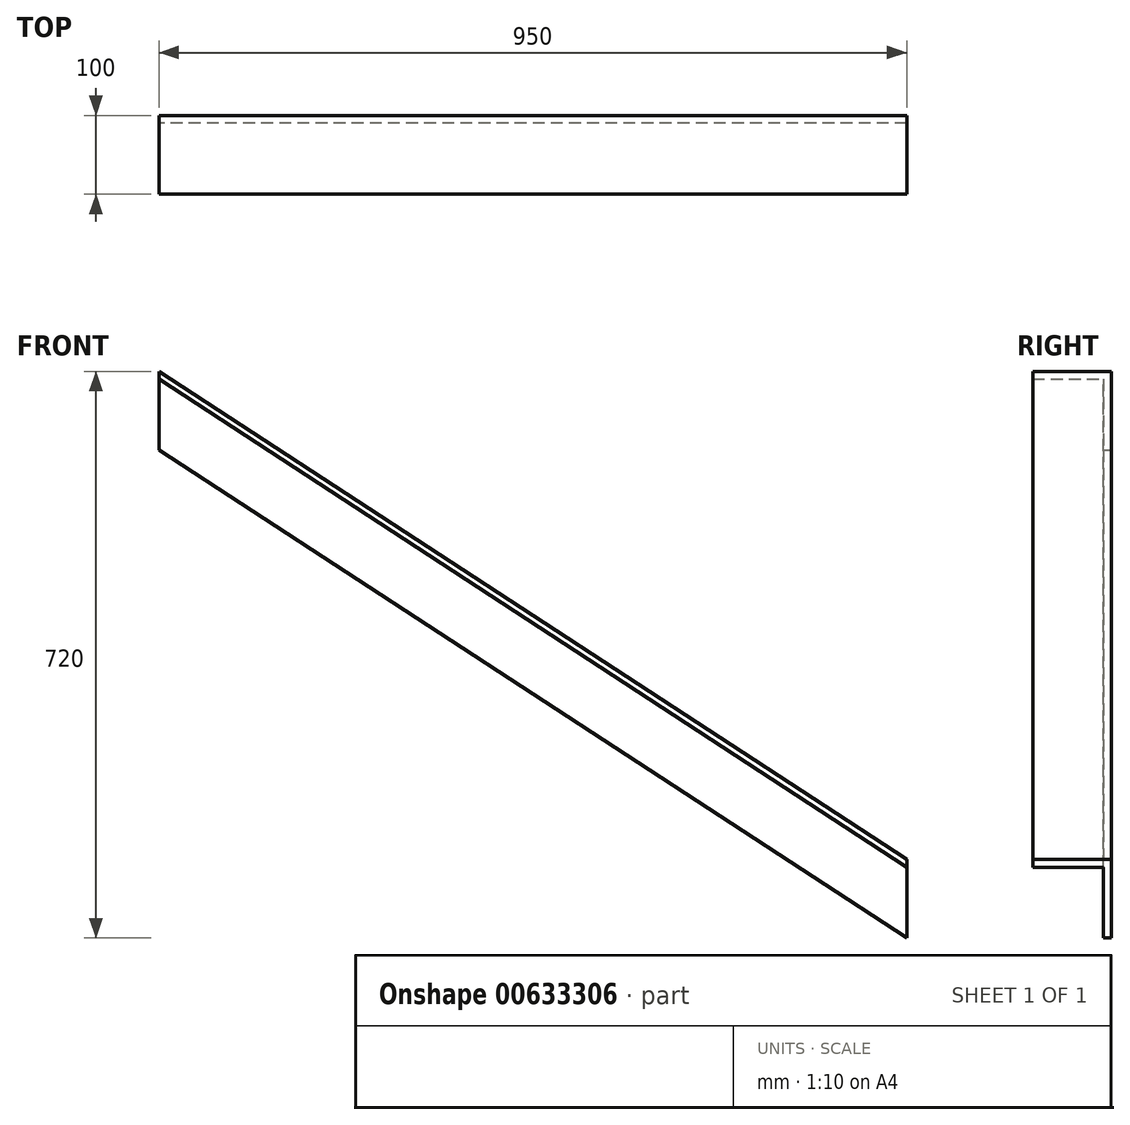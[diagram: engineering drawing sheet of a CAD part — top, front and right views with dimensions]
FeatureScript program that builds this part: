
annotation { "Feature Type Name" : "Feature", "Feature Type Description" : "" }
export const myFeature = defineFeature(function(context is Context, id is Id, definition is map)
    precondition{}
    {
        {
            var Q0;
            Q0=qCreatedBy(makeId("Front.planeOp"),FACE);
            var sketch = newSketch(context, id + "F0", { "sketchPlane" : qUnion([Q0])});
            skLineSegment(sketch, "E0", {"start": v(-500, 500) * mm, "end": v(-500, -500) * mm, "construction": true});
            skLineSegment(sketch, "E1", {"start": v(500, 500) * mm, "end": v(500, -500) * mm, "construction": true});
            skLineSegment(sketch, "E2", {"start": v(-500, 500) * mm, "end": v(500, 500) * mm, "construction": true});
            skLineSegment(sketch, "E3", {"start": v(500, -500) * mm, "end": v(-500, -500) * mm, "construction": true});
            skLineSegment(sketch, "E4", {"start": v(-400, 300) * mm, "end": v(400, 300) * mm, "construction": true});
            skLineSegment(sketch, "E5", {"start": v(400, 300) * mm, "end": v(400, -500) * mm, "construction": true});
            skLineSegment(sketch, "E6", {"start": v(-400, 300) * mm, "end": v(-400, -500) * mm, "construction": true});
            skLineSegment(sketch, "E7", {"start": v(-475, 260) * mm, "end": v(-475, 160) * mm});
            skLineSegment(sketch, "E8", {"start": v(-475, 160) * mm, "end": v(475, -460) * mm});
            skLineSegment(sketch, "E9", {"start": v(475, -460) * mm, "end": v(475, -360) * mm});
            skLineSegment(sketch, "E10", {"start": v(475, -360) * mm, "end": v(-475, 260) * mm});
            skSolve(sketch);
        }
        {
            var Q0;
            Q0 = qSketchRegion(id + "F0", true);
            extrude(context, id + "F1", {"entities" : qUnion([Q0]), "depth" : 10 * mm, "offsetDistance" : 25 * mm});
        }
        {
            var Q0;
            Q0=makeQuery(id+"F1.opExtrude","CAP_FACE",FACE,{"disambiguationData":[OSD([sQuery(id+"F0.wireOp",EDGE,"E7"),sQuery(id+"F0.wireOp",EDGE,"E8"),sQuery(id+"F0.wireOp",EDGE,"E9"),sQuery(id+"F0.wireOp",EDGE,"E10")])],"isStart":false});
            var sketch = newSketch(context, id + "F2", { "sketchPlane" : qUnion([Q0])});
            skLineSegment(sketch, "E11", {"start": v(-475, 260) * mm, "end": v(475, -360) * mm});
            skLineSegment(sketch, "E12", {"start": v(475, -360) * mm, "end": v(475, -370) * mm});
            skLineSegment(sketch, "E13", {"start": v(475, -370) * mm, "end": v(-475, 250) * mm});
            skLineSegment(sketch, "E14", {"start": v(-475, 250) * mm, "end": v(-475, 260) * mm});
            skSolve(sketch);
        }
        {
            var Q0;
            Q0 = qSketchRegion(id + "F2", true);
            extrude(context, id + "F3", {"entities" : qUnion([Q0]), "operationType" : NewBodyOperationType.ADD, "depth" : 90 * mm, "offsetDistance" : 25 * mm});
        }
    });
